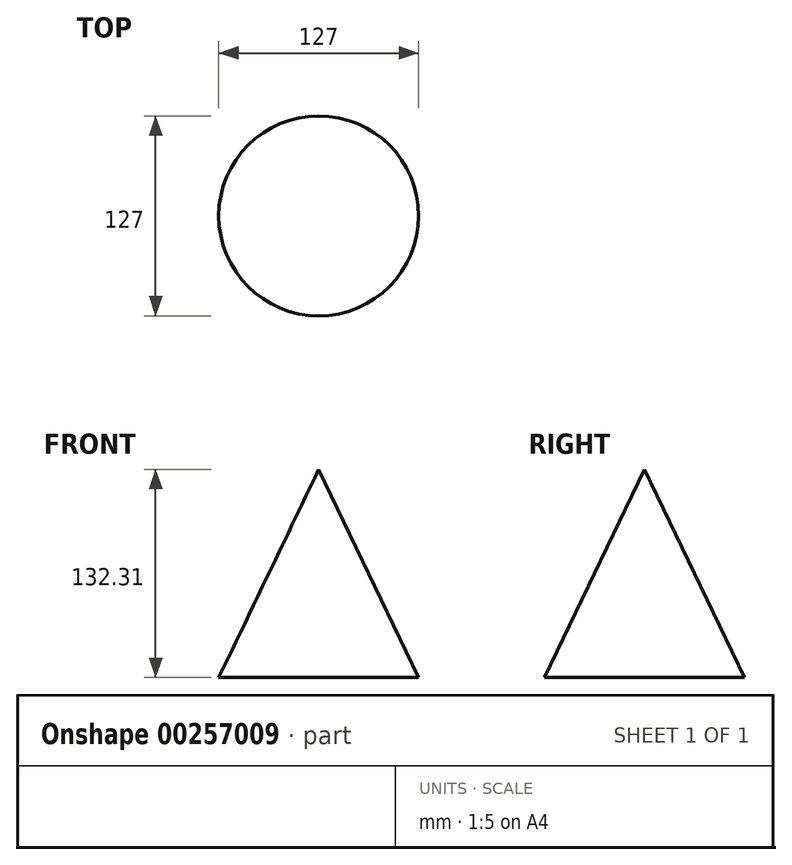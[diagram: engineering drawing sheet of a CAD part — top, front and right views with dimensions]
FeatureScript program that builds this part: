
annotation { "Feature Type Name" : "Feature", "Feature Type Description" : "" }
export const myFeature = defineFeature(function(context is Context, id is Id, definition is map)
    precondition{}
    {
        {
            var Q0;
            Q0=qCreatedBy(makeId("Front.planeOp"),FACE);
            var sketch = newSketch(context, id + "F0", { "sketchPlane" : qUnion([Q0])});
            skLineSegment(sketch, "E0", {"start": v(0, 0) * mm, "end": v(0, 132.3) * mm});
            skLineSegment(sketch, "E1", {"start": v(0, 132.3) * mm, "end": v(63.5, 0) * mm});
            skLineSegment(sketch, "E2", {"start": v(63.5, 0) * mm, "end": v(0, 0) * mm});
            skSolve(sketch);
        }
        {
            var Q0;
            Q0=makeQuery(id+"F0.imprint","IMPRINT",FACE,{"disambiguationData":[TD([[makeQuery(id+"F0.imprint","IMPRINT",EDGE,{"derivedFrom":sQuery(id+"F0.wireOp",EDGE,"E0")}),-1.0]])]});
            var Q1;
            Q1=sQuery(id+"F0.wireOp",EDGE,"E0");
            revolve(context, id + "F1", {"entities" : qUnion([Q0]), "axis" : qUnion([Q1]), "revolveType" : RevolveType.FULL});
        }
    });
